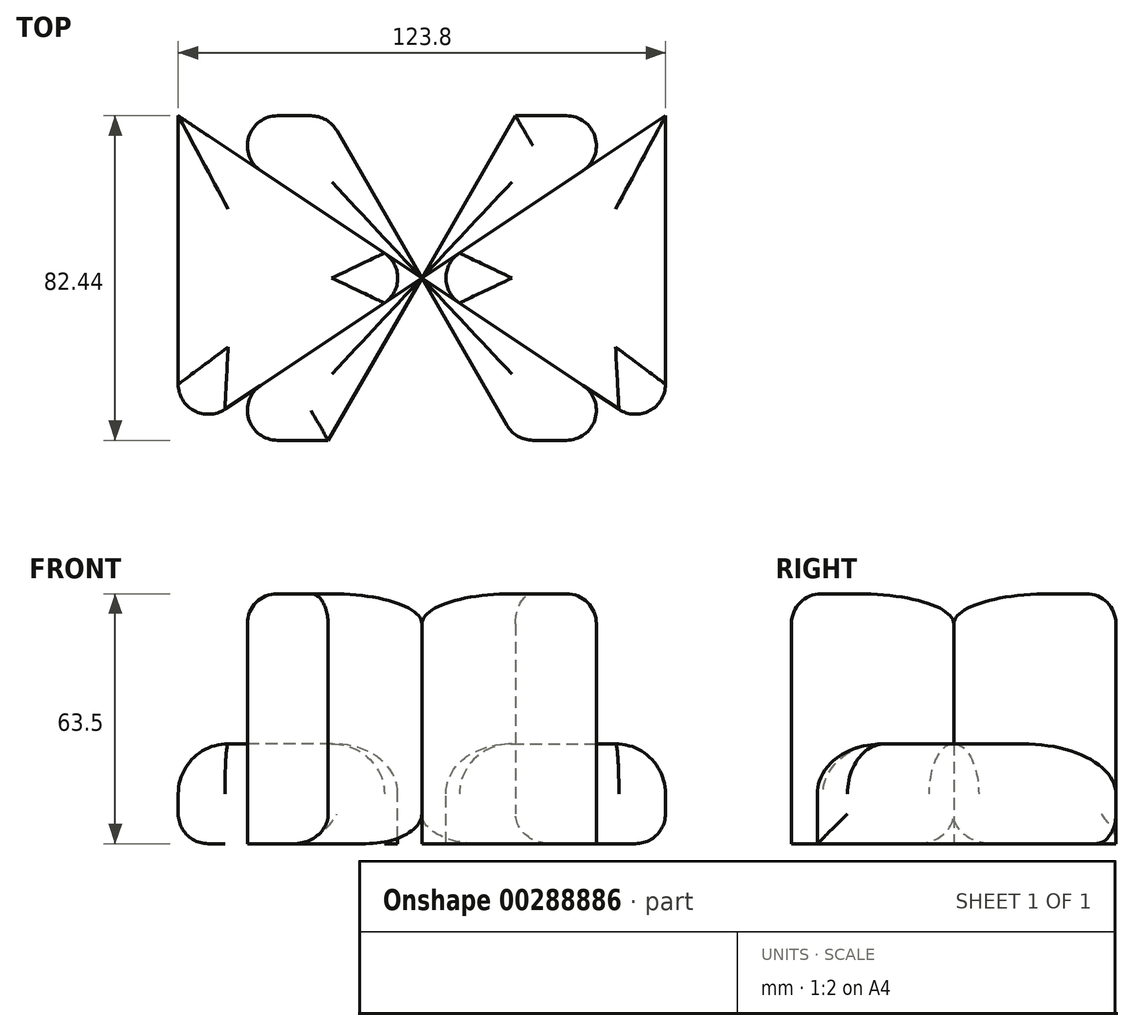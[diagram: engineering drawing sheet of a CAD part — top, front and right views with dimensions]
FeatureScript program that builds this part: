
annotation { "Feature Type Name" : "Feature", "Feature Type Description" : "" }
export const myFeature = defineFeature(function(context is Context, id is Id, definition is map)
    precondition{}
    {
        {
            var Q0;
            Q0=qCreatedBy(makeId("Top.planeOp"),FACE);
            var sketch = newSketch(context, id + "F0", { "sketchPlane" : qUnion([Q0])});
            skLineSegment(sketch, "E0", {"start": v(0, 0) * mm, "end": v(-23.8, 41.22) * mm});
            skLineSegment(sketch, "E1", {"start": v(-23.8, 41.22) * mm, "end": v(-61.9, 41.22) * mm});
            skLineSegment(sketch, "E2", {"start": v(-61.9, 41.22) * mm, "end": v(-61.9, -41.22) * mm});
            skLineSegment(sketch, "E3", {"start": v(-61.9, -41.22) * mm, "end": v(-23.8, -41.22) * mm});
            skLineSegment(sketch, "E4", {"start": v(-23.8, -41.22) * mm, "end": v(0, 0) * mm});
            skLineSegment(sketch, "E5.MirrorCS", {"start": v(0, 0) * mm, "end": v(23.8, 41.22) * mm});
            skLineSegment(sketch, "E6.MirrorCS", {"start": v(23.8, 41.22) * mm, "end": v(61.9, 41.22) * mm});
            skLineSegment(sketch, "E7.MirrorCS", {"start": v(61.9, 41.22) * mm, "end": v(61.9, -41.22) * mm});
            skLineSegment(sketch, "E8.MirrorCS", {"start": v(61.9, -41.22) * mm, "end": v(23.8, -41.22) * mm});
            skLineSegment(sketch, "E9.MirrorCS", {"start": v(23.8, -41.22) * mm, "end": v(0, 0) * mm});
            skLineSegment(sketch, "E10", {"start": v(0, 0) * mm, "end": v(-61.9, 41.22) * mm});
            skLineSegment(sketch, "E11", {"start": v(0, 0) * mm, "end": v(-61.9, -41.22) * mm});
            skLineSegment(sketch, "E12", {"start": v(0, 0) * mm, "end": v(61.9, -41.22) * mm});
            skLineSegment(sketch, "E13", {"start": v(0, 0) * mm, "end": v(61.9, 41.22) * mm});
            skPoint(sketch, "E14.end.orphan", {"position": v(-61.9, 0) * mm});
            skPoint(sketch, "E15.end.orphan", {"position": v(61.9, 0) * mm});
            skSolve(sketch);
        }
        {
            var Q0;
            Q0=makeQuery(id+"F0.imprint","IMPRINT",FACE,{"disambiguationData":[TD([[makeQuery(id+"F0.imprint","IMPRINT",EDGE,{"derivedFrom":sQuery(id+"F0.wireOp",EDGE,"E0")}),1.0]])]});
            var Q1;
            Q1=makeQuery(id+"F0.imprint","IMPRINT",FACE,{"disambiguationData":[TD([[makeQuery(id+"F0.imprint","IMPRINT",EDGE,{"derivedFrom":sQuery(id+"F0.wireOp",EDGE,"E5.MirrorCS")}),-1.0]])]});
            var Q2;
            Q2=makeQuery(id+"F0.imprint","IMPRINT",FACE,{"disambiguationData":[TD([[makeQuery(id+"F0.imprint","IMPRINT",EDGE,{"derivedFrom":sQuery(id+"F0.wireOp",EDGE,"E8.MirrorCS")}),-1.0]])]});
            var Q3;
            Q3=makeQuery(id+"F0.imprint","IMPRINT",FACE,{"disambiguationData":[TD([[makeQuery(id+"F0.imprint","IMPRINT",EDGE,{"derivedFrom":sQuery(id+"F0.wireOp",EDGE,"E3")}),1.0]])]});
            extrude(context, id + "F1", {"entities" : qUnion([Q0, Q1, Q2, Q3]), "depth" : 63.5 * mm});
        }
        {
            var Q0;
            Q0=makeQuery(id+"F0.imprint","IMPRINT",FACE,{"disambiguationData":[TD([[makeQuery(id+"F0.imprint","IMPRINT",EDGE,{"derivedFrom":sQuery(id+"F0.wireOp",EDGE,"E2")}),1.0]])]});
            var Q1;
            Q1=makeQuery(id+"F0.imprint","IMPRINT",FACE,{"disambiguationData":[TD([[makeQuery(id+"F0.imprint","IMPRINT",EDGE,{"derivedFrom":sQuery(id+"F0.wireOp",EDGE,"E7.MirrorCS")}),-1.0]])]});
            extrude(context, id + "F2", {"entities" : qUnion([Q0, Q1]), "depth" : 25.4 * mm});
        }
        {
            var Q0;
            Q0=makeQuery(id+"F1.opExtrude","CAP_EDGE",EDGE,{"disambiguationData":[OSD([sQuery(id+"F0.wireOp",EDGE,"E10")])],"isStart":false});
            var Q1;
            Q1=makeQuery(id+"F1.opExtrude","CAP_EDGE",EDGE,{"disambiguationData":[OSD([sQuery(id+"F0.wireOp",EDGE,"E1")])],"isStart":false});
            var Q2;
            Q2=makeQuery(id+"F1.opExtrude","CAP_EDGE",EDGE,{"disambiguationData":[OSD([sQuery(id+"F0.wireOp",EDGE,"E0")])],"isStart":false});
            var Q3;
            Q3=makeQuery(id+"F1.opExtrude","CAP_EDGE",EDGE,{"disambiguationData":[OSD([sQuery(id+"F0.wireOp",EDGE,"E11")])],"isStart":false});
            var Q4;
            Q4=makeQuery(id+"F1.opExtrude","CAP_EDGE",EDGE,{"disambiguationData":[OSD([sQuery(id+"F0.wireOp",EDGE,"E4")])],"isStart":false});
            var Q5;
            Q5=makeQuery(id+"F1.opExtrude","CAP_EDGE",EDGE,{"disambiguationData":[OSD([sQuery(id+"F0.wireOp",EDGE,"E3")])],"isStart":false});
            var Q6;
            Q6=makeQuery(id+"F1.opExtrude","CAP_EDGE",EDGE,{"disambiguationData":[OSD([sQuery(id+"F0.wireOp",EDGE,"E5.MirrorCS")])],"isStart":false});
            var Q7;
            Q7=makeQuery(id+"F1.opExtrude","CAP_EDGE",EDGE,{"disambiguationData":[OSD([sQuery(id+"F0.wireOp",EDGE,"E6.MirrorCS")])],"isStart":false});
            var Q8;
            Q8=makeQuery(id+"F1.opExtrude","CAP_EDGE",EDGE,{"disambiguationData":[OSD([sQuery(id+"F0.wireOp",EDGE,"E13")])],"isStart":false});
            var Q9;
            Q9=makeQuery(id+"F1.opExtrude","CAP_EDGE",EDGE,{"disambiguationData":[OSD([sQuery(id+"F0.wireOp",EDGE,"E9.MirrorCS")])],"isStart":false});
            var Q10;
            Q10=makeQuery(id+"F1.opExtrude","CAP_EDGE",EDGE,{"disambiguationData":[OSD([sQuery(id+"F0.wireOp",EDGE,"E12")])],"isStart":false});
            var Q11;
            Q11=makeQuery(id+"F1.opExtrude","CAP_EDGE",EDGE,{"disambiguationData":[OSD([sQuery(id+"F0.wireOp",EDGE,"E8.MirrorCS")])],"isStart":false});
            var Q12;
            Q12=makeQuery(id+"F2.opExtrude","CAP_EDGE",EDGE,{"disambiguationData":[OSD([sQuery(id+"F0.wireOp",EDGE,"E7.MirrorCS")])],"isStart":true});
            var Q13;
            Q13=makeQuery(id+"F2.opExtrude","SWEPT_EDGE",EDGE,{"disambiguationData":[OSD([sQuery(id+"F0.wireOp",EDGE,"E7.MirrorCS"),sQuery(id+"F0.wireOp",EDGE,"E8.MirrorCS"),sQuery(id+"F0.wireOp",EDGE,"E12")])]});
            var Q14;
            Q14=makeQuery(id+"F1.opExtrude","SWEPT_EDGE",EDGE,{"disambiguationData":[OSD([sQuery(id+"F0.wireOp",EDGE,"E6.MirrorCS"),sQuery(id+"F0.wireOp",EDGE,"E7.MirrorCS"),sQuery(id+"F0.wireOp",EDGE,"E13")])]});
            var Q15;
            Q15=makeQuery(id+"F1.opExtrude","SWEPT_EDGE",EDGE,{"disambiguationData":[OSD([sQuery(id+"F0.wireOp",EDGE,"E7.MirrorCS"),sQuery(id+"F0.wireOp",EDGE,"E8.MirrorCS"),sQuery(id+"F0.wireOp",EDGE,"E12")])]});
            var Q16;
            Q16=makeQuery(id+"F1.opExtrude","SWEPT_EDGE",EDGE,{"disambiguationData":[OSD([sQuery(id+"F0.wireOp",EDGE,"E8.MirrorCS"),sQuery(id+"F0.wireOp",EDGE,"E9.MirrorCS")])]});
            var Q17;
            Q17=makeQuery(id+"F1.opExtrude","SWEPT_EDGE",EDGE,{"disambiguationData":[OSD([sQuery(id+"F0.wireOp",EDGE,"E2"),sQuery(id+"F0.wireOp",EDGE,"E3"),sQuery(id+"F0.wireOp",EDGE,"E11")])]});
            var Q18;
            Q18=makeQuery(id+"F1.opExtrude","SWEPT_EDGE",EDGE,{"disambiguationData":[OSD([sQuery(id+"F0.wireOp",EDGE,"E0"),sQuery(id+"F0.wireOp",EDGE,"E1")])]});
            var Q19;
            {var subQ0=sQuery(id+"F0.wireOp",EDGE,"E13");var subQ1=sQuery(id+"F0.wireOp",EDGE,"E12");Q19=makeQuery(id+"F2.opExtrude","SWEPT_EDGE",EDGE,{"disambiguationData":[OSD([sQuery(id+"F0.wireOp",EDGE,"E0"),sQuery(id+"F0.wireOp",EDGE,"E4"),sQuery(id+"F0.wireOp",EDGE,"E5.MirrorCS"),sQuery(id+"F0.wireOp",EDGE,"E9.MirrorCS"),sQuery(id+"F0.wireOp",EDGE,"E10"),sQuery(id+"F0.wireOp",EDGE,"E11"),subQ1,subQ0]),ownerDisambiguation([makeQuery(id+"F2.opExtrude","SWEPT_BODY",BODY,{"disambiguationData":[OSD([sQuery(id+"F0.wireOp",EDGE,"E7.MirrorCS"),subQ1,subQ0])]})])]});}
            var Q20;
            Q20=makeQuery(id+"F2.opExtrude","CAP_EDGE",EDGE,{"disambiguationData":[OSD([sQuery(id+"F0.wireOp",EDGE,"E2")])],"isStart":true});
            var Q21;
            Q21=makeQuery(id+"F1.opExtrude","CAP_EDGE",EDGE,{"disambiguationData":[OSD([sQuery(id+"F0.wireOp",EDGE,"E4")])],"isStart":true});
            var Q22;
            Q22=makeQuery(id+"F1.opExtrude","CAP_EDGE",EDGE,{"disambiguationData":[OSD([sQuery(id+"F0.wireOp",EDGE,"E5.MirrorCS")])],"isStart":true});
            var Q23;
            Q23=makeQuery(id+"F1.opExtrude","CAP_EDGE",EDGE,{"disambiguationData":[OSD([sQuery(id+"F0.wireOp",EDGE,"E0")])],"isStart":true});
            var Q24;
            Q24=makeQuery(id+"F2.opExtrude","SWEPT_EDGE",EDGE,{"disambiguationData":[OSD([sQuery(id+"F0.wireOp",EDGE,"E2"),sQuery(id+"F0.wireOp",EDGE,"E3"),sQuery(id+"F0.wireOp",EDGE,"E11")])]});
            var Q25;
            Q25=makeQuery(id+"F1.opExtrude","SWEPT_EDGE",EDGE,{"disambiguationData":[OSD([sQuery(id+"F0.wireOp",EDGE,"E1"),sQuery(id+"F0.wireOp",EDGE,"E2"),sQuery(id+"F0.wireOp",EDGE,"E10")])]});
            fillet(context, id + "F3", {"entities" : qUnion([Q0, Q1, Q2, Q3, Q4, Q5, Q6, Q7, Q8, Q9, Q10, Q11, Q12, Q13, Q14, Q15, Q16, Q17, Q18, Q19, Q20, Q21, Q22, Q23, Q24, Q25]), "radius" : 7.62 * mm, "tangentPropagation" : true, "allowEdgeOverflow" : false});
        }
        {
            var Q0;
            Q0=makeQuery(id+"F2.opExtrude","CAP_EDGE",EDGE,{"disambiguationData":[OSD([sQuery(id+"F0.wireOp",EDGE,"E2")])],"isStart":false});
            var Q1;
            Q1=makeQuery(id+"F2.opExtrude","CAP_EDGE",EDGE,{"disambiguationData":[OSD([sQuery(id+"F0.wireOp",EDGE,"E11")])],"isStart":false});
            var Q2;
            Q2=makeQuery(id+"F2.opExtrude","CAP_EDGE",EDGE,{"disambiguationData":[OSD([sQuery(id+"F0.wireOp",EDGE,"E10")])],"isStart":false});
            var Q3;
            Q3=makeQuery(id+"F2.opExtrude","CAP_EDGE",EDGE,{"disambiguationData":[OSD([sQuery(id+"F0.wireOp",EDGE,"E2")])],"isStart":true});
            var Q4;
            Q4=makeQuery(id+"F2.opExtrude","CAP_EDGE",EDGE,{"disambiguationData":[OSD([sQuery(id+"F0.wireOp",EDGE,"E13")])],"isStart":false});
            var Q5;
            Q5=makeQuery(id+"F2.opExtrude","CAP_EDGE",EDGE,{"disambiguationData":[OSD([sQuery(id+"F0.wireOp",EDGE,"E7.MirrorCS")])],"isStart":false});
            var Q6;
            Q6=makeQuery(id+"F2.opExtrude","CAP_EDGE",EDGE,{"disambiguationData":[OSD([sQuery(id+"F0.wireOp",EDGE,"E12")])],"isStart":false});
            fillet(context, id + "F4", {"entities" : qUnion([Q0, Q1, Q2, Q3, Q4, Q5, Q6]), "radius" : 12.7 * mm, "tangentPropagation" : true, "allowEdgeOverflow" : false});
        }
    });
